# Revit family: Sirius_two_FS_90kW_LOD-5
name_source: partatom
category: Mechanical Equipment
revit_build: Autodesk Revit 2014 (Build: 20140709_2115(x64)
units: mm (PartAtom-declared; Revit-internal decimal feet)

## types (1)
- 90kW
    6 Monthly = 0
    Access Clearance Bottom = 0 mm
    Access Clearance Front = 1000 mm
    Access Clearance Left = 500 mm
    Access Clearance Rear = 500 mm
    Access Clearance Right = 500 mm
    Access Clearance Top = 250 mm
    Additional Technical Details = Cascade kits available for up to 6 boilers
    Air Inlet Connection Size = 160 mm
    Annually = Annual service according to manufacturers guidance.
    BMS Links = Yes
    Bespoke Timeframe = 0
    Building Regulations Seasonal Efficiency = 96.8 %
    Burner Control Type = Modulating
    CE Mark = CE-0085CP0089
    Colour = White
    Condensate Drain Size = 22 mm
    Condensate Drain Type = Plain
    Configuration = Single boiler
    Control Type = Optimised, modulating, weather compensating, BMS compatible
    Daily = 0
    Drain Connection Size = 0 mm
    Drain Connection Type = Plain
    Embodied Carbon = 0
    Energy Technology List = https://etl.decc.gov.uk
    Environmental Product Declaration = 0
    ErP Energy Label = 0
    ErP Rated Efficiency at Full Load = 87.7 %
    ErP Rated Efficiency at Part Load = 97.5 %
    ErP Seasonal Efficiency = 0 %
    Expected Life = >10 years
    External Material = Steel
    Features = Floor standing boiler, stainless steel heat exchanger, 9:1 modulation
    Finish = Powder coated
    Flow and Return Connection Size = 968 mm
    Flow and Return Connection Type = Threaded
    Flue Connection size = 110 mm
    Flue or Air Intake Classification = C13; C33; B23; B23p; C43; C53; C63; C83
    Frequency = 50 Hz
    Fuel Connection Size = 645 mm
    Fuel Connection Type = Threaded
    Full Load Current = 0 A
    Fuse Rating = 0 A
    Gas Consumption rate = 9.25 m3/h
    Green Guide for Specification = 0
    Gross Weight = 104.00 kg
    Heat Exchanger Material = Stainless Steel
    Heater Operation = Condensing
    Hydraulic Resistance at 11C temperature differential = 0.040
    Hydraulic Resistance at 20C temperature differential = 0.022
    IK Rating = 0
    IP Rating = IP21
    IfcExportAs = IfcBoilerType
    IfcExportType = NOTDEFINED
    Interlocks = Yes
    Life Cycle Analysis = 0
    Location of Manufacturer = 0
    Maintenance Required 0 to 300hrs = 0
    Maintenance Required 1001 to 2000hrs = 0
    Maintenance Required 2001 to 4000hrs = 0
    Maintenance Required 301 to 600hrs = 0
    Maintenance Required 4001 to 8000hrs = 0
    Maintenance Required 601 to 1000hrs = 0
    Maintenance Required 8001 to 12000hrs = 0
    Manufacturer = Potterton Commercial
    Manufacturer Website = http://www.pottertoncommercial.co.uk
    Material Ingredient Reporting = 0
    Maximum Gas Inlet Pressure = 0.000 bar
    Maximum Oil Inlet Pressure = 0.000 bar
    Maximum Operating Pressure = 4.000 bar
    Maximum Power Consumption = 146 W
    Minimum Flow Rate at 11C temperature differential = 1.360 L/s
    Minimum Flow Rate at 20C temperature differential = 1.020 L/s
    Minimum Gas Inlet Pressure = 0.018 bar
    Minimum Oil Inlet Pressure = 0.000 bar
    Minimum Operating Pressure = 1.000 bar
    Minimum Power Consumption = 24 W
    Model = SIRIUS two FS50
    Monthly = 0
    Mounting = Floor Standing
    NOx Emissions = 36 mg/kWh
    Nominal Gas Inlet Pressure = 0.020 bar
    Nominal Oil Inlet Pressure = 0.000 bar
    Oil Consumption rate = 0
    Operation and Maintenance Manual = http://www.pottertoncommercial.co.uk
    Optional Fuel = Gas - LPG
    Overall Height = 1127 mm
    Overall Length = 681 mm
    Overall Width = 600 mm
    Primary Fuel = Gas - NG
    Product Literature = ww.pottertoncommercial.co.uk/products/stainless-steel/sirius-two-fs-50-110kW.htm
    Product Model Number = 5142182
    Product Range = Sirius two FS (90kW)
    Quarterly = 0
    Rated Criteria = 80/60
    Rated Output = 85000 W
    Reference Standard = ISO 9001; ISO 14001
    Responsible Extraction of Materials = 0
    Responsible Sourcing of Materials = 0
    Safety Valve Connection Size = 19 mm
    Safety Valve Connection Type = Threaded
    Shape = Rectangular (Vertical)
    Shipping Weight = 117.00 kg
    Sound Pressure Level = 64 dBA
    Starting Current = 0 A
    Supply Phase = 1
    Turndown Ratio = 9:1
    Uniclass2015 = Pr_60_60_08
    Voltage = 230 V
    Warranty ID = See manufacturers website for warranty options and T&C's
    Water Content = 8.3 L
    Water Treatment Required = Yes
    Weekly = 0

note: source unit labels omitted for Hydraulic Resistance at 11C temperature differential, Hydraulic Resistance at 20C temperature differential — the stored unit's dimension contradicts the parameter name (converter mislabeling)

## geometry (parser evidence)
native form markers: Blend x6, Extrusion x1, Sweep x3
no freeform markers — native parametric forms only
